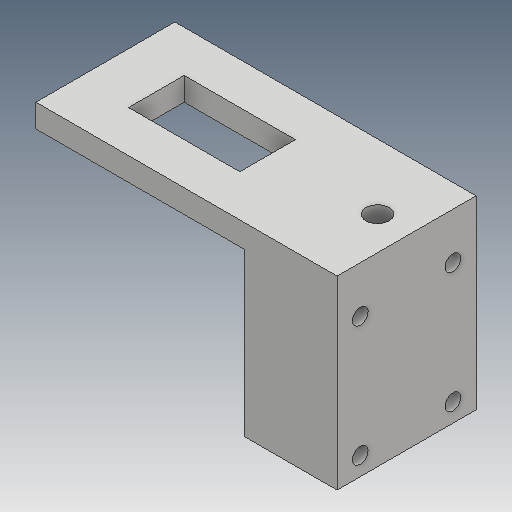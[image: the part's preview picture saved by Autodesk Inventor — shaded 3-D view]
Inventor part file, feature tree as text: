
AUTODESK INVENTOR PART (.ipt)
format: ipt  version: 2018 (Build 220112000, 112)  size: 141,312 bytes
history: native  units: mm
features: sketch x5, extrude x4, other x4, reference x1
ambient origin geometry x8: Origin, YZ Plane, XZ Plane, XY Plane, X Axis, Y Axis, Z Axis, Center Point
bodies: Volumenkörper1 (feature_tree)
feature tree (14):
  sketch  "Skizze1"  dims[d0=5.0mm d1=20.0mm]
  extrude  "Extrusion1"  Depth=20.0mm
  extrude  "Extrusion2"  Depth=30.0mm TaperAngle=0.0deg
  sketch  "Skizze3"  dims[d5=65.0mm d6=30.0mm]
  extrude  "Extrusion3"  Depth=30.0mm
  sketch  "Skizze4"  dims[d7=24.0mm d8=12.0mm]
  extrude  "Extrusion4"  Depth=12.0mm
  sketch  "Skizze2"  dims[d2=40.0mm d3=30.0mm d4=0.0mm]
  sketch  "Skizze5"  dims[d9=9.0mm d10=5.0mm d11=0.0mm d12=3.4mm d13=3.4mm d14=3.4mm d15=3.4mm d16=10.0mm d17=20.0mm d18=5.0mm d19=10.0mm d20=4.0mm d21=20.0mm d22=4.0mm d23=5.0mm d24=20.0mm d25=0.0mm d26=5.0mm d27=10.0mm d28=0.0mm]
  reference  "Referenz1"
  other  "<userpath>\OneDrive\Development\RTW\03_Konstruktion\StirnradUNDServo.iam"
  other  "StirnradUNDServo.iam"
  other  "Stirnräder:1"
  other  "Stirnzahnrad1:1"
